# Revit family: NORFAC - Door Family template
name_source: partatom
category: Doors
revit_build: Autodesk Revit 2017 (Build: 20160225_1515(x64)
units: mm (PartAtom-declared; Revit-internal decimal feet)

## family parameters
Always vertical = Yes
Cut with Voids When Loaded = No
Host = Wall
OmniClass Number = 23.30.10.00
OmniClass Title = Doors
Room Calculation Point = No
Shared = No

## types (1)
- NORFAC - Door Family template
    Door Area = 1.93 m²
    Door Sheet Recess in Frame = 20 mm  [stored 0.0656168 ft]
    Door Sheet Thickness = 40 mm  [stored 0.131234 ft]
    Eref Energy Balance = 0
    Ew East = 0
    Ew North = 0
    Ew South = 0
    Ew West = 0
    Frame Area = 0.55 m²
    Frame Depth = 60 mm  [stored 0.19685 ft]
    Frame Width = 100 mm  [stored 0.328084 ft]
    Function = Interior
    Glass Area = 1.38 m²
    Glass Distance Bottom = 100 mm  [stored 0.328084 ft]
    Glass Distance Side = 100 mm  [stored 0.328084 ft]
    Glass Distance Top = 100 mm  [stored 0.328084 ft]
    Glass Height = 1776 mm
    Glass Recess in Door  Sheet = 10 mm  [stored 0.0328084 ft]
    Glass Thickness = 20 mm  [stored 0.0656168 ft]
    Glass Width = 776 mm
    Height = 1976 mm
    Include in PhPP = Yes
    Insert in Wall = 200 mm  [stored 0.656168 ft]
    Joint = 12 mm  [stored 0.0393701 ft]
    LT value = 1
    Psi Glass = 0
    Rough Height = 2000 mm  [stored 6.56168 ft]
    Rough Width = 1000 mm  [stored 3.28084 ft]
    U value = 0
    U value Frame = 0
    U value Glass = 0
    Wall Closure = By host
    Width = 976 mm
    g value = 0
    gw = 0

note: [stored X ft] marks values corroborated as IEEE doubles in the binary element streams (Revit-internal decimal feet)

## geometry (parser evidence)
native form markers: Sweep x1
no freeform markers — native parametric forms only
